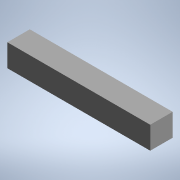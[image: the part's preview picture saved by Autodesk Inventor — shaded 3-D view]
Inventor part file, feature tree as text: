
AUTODESK INVENTOR PART (.ipt)
format: ipt  version: 2020 (Build 240168000, 168)  size: 88,064 bytes
history: native  units: mm
features: other x3, extrude x1, sketch x1, reference x1
ambient origin geometry x8: Origin, YZ Plane, XZ Plane, XY Plane, X Axis, Y Axis, Z Axis, Center Point
bodies: 实体1 (feature_tree)
feature tree (6):
  extrude  "拉伸1"  [1 undecoded]
  sketch  "草图1"  dims[d0=22.0mm d1=0.0mm]
  reference  "参考1"
  other  "<userpath>\Desktop\装配3\Workspace\cpz assemble.iam"
  other  "cpz assemble.iam"
  other  "轴:2"
note: 1 required parameter value undecoded (feature->parameter linkage not recoverable at this tier; creation-order binding heuristic only, values carry confidence <= 0.55)
